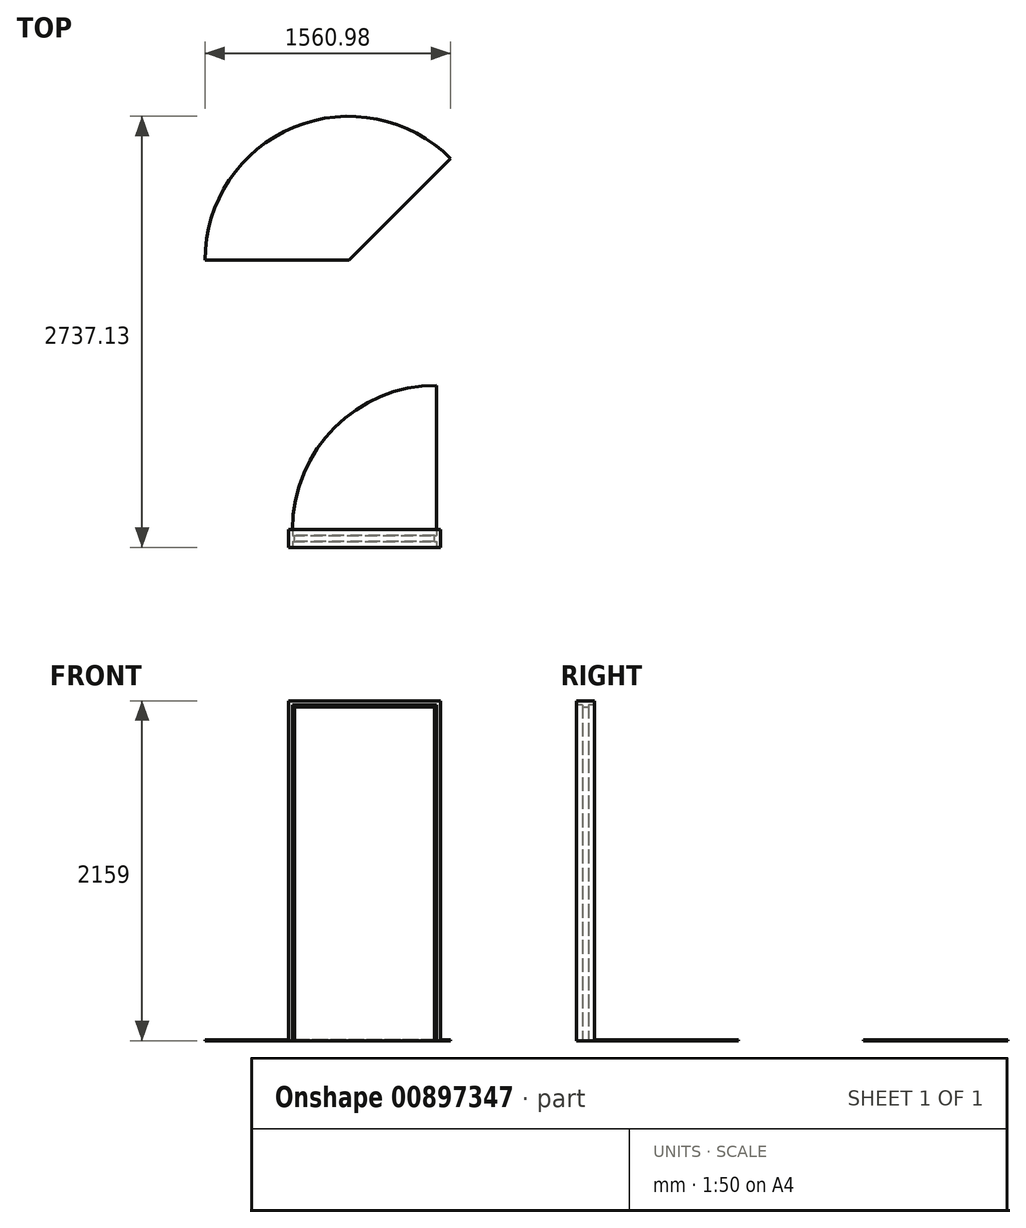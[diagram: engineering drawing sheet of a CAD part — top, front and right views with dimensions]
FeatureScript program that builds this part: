
annotation { "Feature Type Name" : "Feature", "Feature Type Description" : "" }
export const myFeature = defineFeature(function(context is Context, id is Id, definition is map)
    precondition{}
    {
        {
            var Q0;
            Q0=qCreatedBy(makeId("Top.planeOp"),FACE);
            var sketch = newSketch(context, id + "F0", { "sketchPlane" : qUnion([Q0])});
            skLineSegment(sketch, "E0.bottom", {"start": v(939.8, 57.15) * mm, "end": v(965.2, 57.15) * mm});
            skLineSegment(sketch, "E0.top", {"start": v(939.8, -57.15) * mm, "end": v(965.2, -57.15) * mm});
            skLineSegment(sketch, "E0.left", {"start": v(939.8, 57.15) * mm, "end": v(939.8, -57.15) * mm});
            skLineSegment(sketch, "E0.right", {"start": v(965.2, 57.15) * mm, "end": v(965.2, -57.15) * mm});
            skLineSegment(sketch, "E1.bottom", {"start": v(0, 57.15) * mm, "end": v(25.4, 57.15) * mm});
            skLineSegment(sketch, "E1.top", {"start": v(0, -57.15) * mm, "end": v(25.4, -57.15) * mm});
            skLineSegment(sketch, "E1.left", {"start": v(0, 57.15) * mm, "end": v(0, -57.15) * mm});
            skLineSegment(sketch, "E1.right", {"start": v(25.4, 57.15) * mm, "end": v(25.4, -57.15) * mm});
            skLineSegment(sketch, "E2.bottom", {"start": v(25.4, 19.05) * mm, "end": v(38.1, 19.05) * mm});
            skLineSegment(sketch, "E2.top", {"start": v(25.4, -19.05) * mm, "end": v(38.1, -19.05) * mm});
            skLineSegment(sketch, "E2.left", {"start": v(25.4, 19.05) * mm, "end": v(25.4, -19.05) * mm});
            skLineSegment(sketch, "E2.right", {"start": v(38.1, 19.05) * mm, "end": v(38.1, -19.05) * mm});
            skPoint(sketch, "E3", {"position": v(25.4, 0) * mm});
            skLineSegment(sketch, "E4.bottom", {"start": v(927.1, 19.05) * mm, "end": v(939.8, 19.05) * mm});
            skLineSegment(sketch, "E4.top", {"start": v(927.1, -19.05) * mm, "end": v(939.8, -19.05) * mm});
            skLineSegment(sketch, "E4.left", {"start": v(927.1, 19.05) * mm, "end": v(927.1, -19.05) * mm});
            skLineSegment(sketch, "E4.right", {"start": v(939.8, 19.05) * mm, "end": v(939.8, -19.05) * mm});
            skPoint(sketch, "E5", {"position": v(939.8, 0) * mm});
            skLineSegment(sketch, "E6.bottom", {"start": v(25.4, 57.15) * mm, "end": v(939.8, 57.15) * mm});
            skLineSegment(sketch, "E6.top", {"start": v(25.4, 19.05) * mm, "end": v(939.8, 19.05) * mm});
            skLineSegment(sketch, "E6.left", {"start": v(25.4, 57.15) * mm, "end": v(25.4, 19.05) * mm});
            skLineSegment(sketch, "E6.right", {"start": v(939.8, 57.15) * mm, "end": v(939.8, 19.05) * mm});
            skArc(sketch, "E7", {"start": v(939.8, 971.55) * mm, "mid": v(293.22, 703.73) * mm, "end": v(25.4, 57.15) * mm});
            skLineSegment(sketch, "E8", {"start": v(939.8, 57.15) * mm, "end": v(939.8, 971.55) * mm});
            skLineSegment(sketch, "E9.bottom", {"start": v(-530.77, 1765.58) * mm, "end": v(383.63, 1765.58) * mm});
            skArc(sketch, "E10", {"start": v(1030.21, 2412.16) * mm, "mid": v(33.7, 2610.38) * mm, "end": v(-530.77, 1765.58) * mm});
            skLineSegment(sketch, "E11", {"start": v(383.63, 1765.58) * mm, "end": v(1030.21, 2412.16) * mm});
            skSolve(sketch);
        }
        {
            var Q0;
            {var subQ3=sQuery(id+"F0.wireOp",EDGE,"E1.bottom");Q0=makeQuery(id+"F0.imprint","IMPRINT",FACE,{"disambiguationData":[TD([[makeQuery(id+"F0.imprint","IMPRINT",EDGE,{"derivedFrom":subQ3}),-1.0]])]});}
            var Q1;
            {var subQ2=sQuery(id+"F0.wireOp",EDGE,"E2.bottom");Q1=makeQuery(id+"F0.imprint","IMPRINT",FACE,{"disambiguationData":[TD([[makeQuery(id+"F0.imprint","IMPRINT",EDGE,{"derivedFrom":subQ2}),-1.0]])]});}
            var Q2;
            {var subQ1=sQuery(id+"F0.wireOp",EDGE,"E0.bottom");Q2=makeQuery(id+"F0.imprint","IMPRINT",FACE,{"disambiguationData":[TD([[makeQuery(id+"F0.imprint","IMPRINT",EDGE,{"derivedFrom":subQ1}),-1.0]])]});}
            var Q3;
            {var subQ2=sQuery(id+"F0.wireOp",EDGE,"E4.bottom");Q3=makeQuery(id+"F0.imprint","IMPRINT",FACE,{"disambiguationData":[TD([[makeQuery(id+"F0.imprint","IMPRINT",EDGE,{"derivedFrom":subQ2}),-1.0]])]});}
            extrude(context, id + "F1", {"entities" : qUnion([Q0, Q1, Q2, Q3]), "depth" : 2133.6 * mm, "offsetDistance" : 25.4 * mm});
        }
        {
            var Q0;
            Q0=makeQuery(id+"F1.opExtrude","SWEPT_FACE",FACE,{"disambiguationData":[OSD([sQuery(id+"F0.wireOp",EDGE,"E1.left")])]});
            var sketch = newSketch(context, id + "F2", { "sketchPlane" : qUnion([Q0])});
            skLineSegment(sketch, "E12.bottom", {"start": v(-57.15, 2159) * mm, "end": v(57.15, 2159) * mm});
            skLineSegment(sketch, "E12.top", {"start": v(-57.15, 2133.6) * mm, "end": v(57.15, 2133.6) * mm});
            skLineSegment(sketch, "E12.left", {"start": v(-57.15, 2159) * mm, "end": v(-57.15, 2133.6) * mm});
            skLineSegment(sketch, "E12.right", {"start": v(57.15, 2159) * mm, "end": v(57.15, 2133.6) * mm});
            skLineSegment(sketch, "E13.bottom", {"start": v(-19.05, 2133.6) * mm, "end": v(19.05, 2133.6) * mm});
            skLineSegment(sketch, "E13.top", {"start": v(-19.05, 2120.9) * mm, "end": v(19.05, 2120.9) * mm});
            skLineSegment(sketch, "E13.left", {"start": v(-19.05, 2133.6) * mm, "end": v(-19.05, 2120.9) * mm});
            skLineSegment(sketch, "E13.right", {"start": v(19.05, 2133.6) * mm, "end": v(19.05, 2120.9) * mm});
            skPoint(sketch, "E14", {"position": v(0, 2133.6) * mm});
            skSolve(sketch);
        }
        {
            var Q0;
            Q0=makeQuery(id+"F2.imprint","IMPRINT",FACE,{"disambiguationData":[TD([[makeQuery(id+"F2.imprint","IMPRINT",EDGE,{"derivedFrom":sQuery(id+"F2.wireOp",EDGE,"E13.top")}),1.0]])]});
            var Q1;
            Q1=makeQuery(id+"F2.imprint","IMPRINT",FACE,{"disambiguationData":[TD([[makeQuery(id+"F2.imprint","IMPRINT",EDGE,{"derivedFrom":sQuery(id+"F2.wireOp",EDGE,"E12.bottom")}),-1.0]])]});
            extrude(context, id + "F3", {"entities" : qUnion([Q0, Q1]), "operationType" : NewBodyOperationType.ADD, "oppositeDirection" : true, "depth" : 965.2 * mm, "offsetDistance" : 25.4 * mm});
        }
        {
            var Q0;
            {var subQ1=sQuery(id+"F0.wireOp",EDGE,"E2.bottom");Q0=makeQuery(id+"F0.imprint","IMPRINT",FACE,{"disambiguationData":[TD([[makeQuery(id+"F0.imprint","IMPRINT",EDGE,{"derivedFrom":subQ1}),1.0]])]});}
            extrude(context, id + "F4", {"entities" : qUnion([Q0]), "depth" : 2133.6 * mm, "offsetDistance" : 25.4 * mm});
        }
        {
            var Q0;
            Q0=makeQuery(id+"F0.imprint","IMPRINT",FACE,{"disambiguationData":[TD([[makeQuery(id+"F0.imprint","IMPRINT",EDGE,{"derivedFrom":sQuery(id+"F0.wireOp",EDGE,"E6.bottom")}),1.0]])]});
            var Q1;
            Q1=makeQuery(id+"F0.imprint","IMPRINT",FACE,{"disambiguationData":[TD([[makeQuery(id+"F0.imprint","IMPRINT",EDGE,{"derivedFrom":sQuery(id+"F0.wireOp",EDGE,"E9.bottom")}),1.0]])]});
            extrude(context, id + "F5", {"entities" : qUnion([Q0, Q1]), "depth" : 6.35 * mm, "offsetDistance" : 25.4 * mm});
        }
    });
